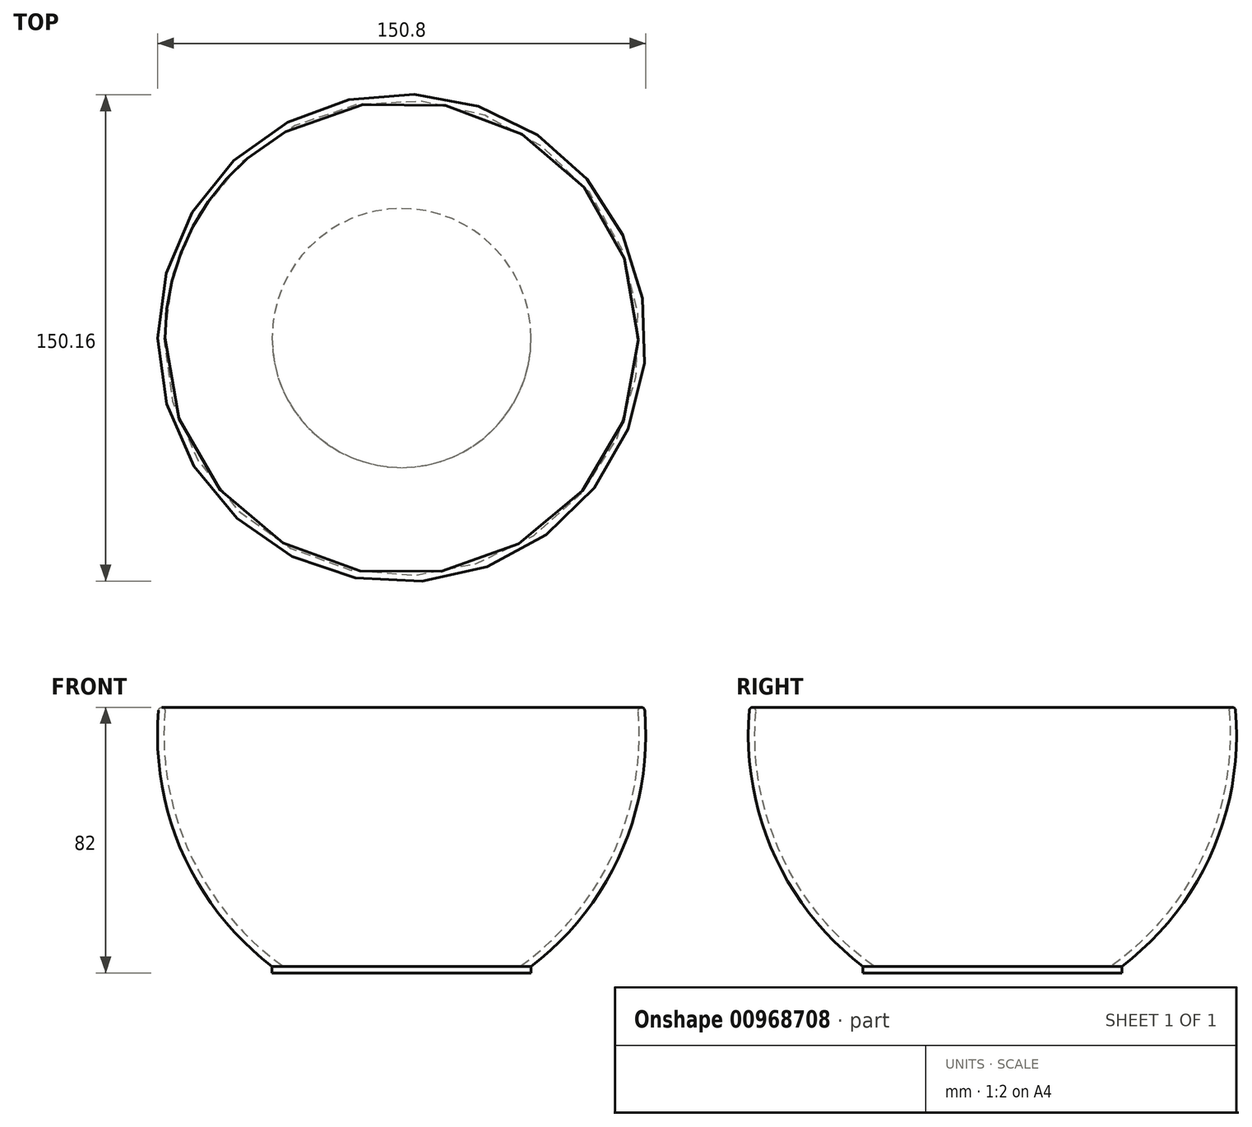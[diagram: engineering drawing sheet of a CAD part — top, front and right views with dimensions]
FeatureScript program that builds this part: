
annotation { "Feature Type Name" : "Feature", "Feature Type Description" : "" }
export const myFeature = defineFeature(function(context is Context, id is Id, definition is map)
    precondition{}
    {
        {
            var Q0;
            Q0=qCreatedBy(makeId("Front.planeOp"),FACE);
            var sketch = newSketch(context, id + "F0", { "sketchPlane" : qUnion([Q0])});
            skLineSegment(sketch, "E0.bottom", {"start": v(0, -82) * mm, "end": v(-40, -82) * mm});
            skLineSegment(sketch, "E0.top", {"start": v(0, -80) * mm, "end": v(-40, -80) * mm});
            skLineSegment(sketch, "E0.left", {"start": v(0, -82) * mm, "end": v(0, -80) * mm});
            skLineSegment(sketch, "E0.right", {"start": v(-40, -82) * mm, "end": v(-40, -80) * mm});
            skLineSegment(sketch, "E1", {"start": v(0, 0) * mm, "end": v(-75, 0) * mm, "construction": true});
            skArc(sketch, "E2", {"start": v(-75, 0) * mm, "mid": v(-67.85, -44.53) * mm, "end": v(-40, -80) * mm});
            skLineSegment(sketch, "E3", {"start": v(0, 0) * mm, "end": v(0, -87.47) * mm, "construction": true});
            skArc(sketch, "E4.0", {"start": v(-73, 0) * mm, "mid": v(-65.51, -44.86) * mm, "end": v(-36.64, -80) * mm});
            skLineSegment(sketch, "E5", {"start": v(-73, 0) * mm, "end": v(-75, 0) * mm});
            skSolve(sketch);
        }
        {
            var Q0;
            {var subQ0=sQuery(id+"F0.wireOp",EDGE,"E2");Q0=makeQuery(id+"F0.imprint","IMPRINT",FACE,{"disambiguationData":[TD([[makeQuery(id+"F0.imprint","IMPRINT",EDGE,{"derivedFrom":subQ0}),1.0]])]});}
            var Q1;
            Q1=makeQuery(id+"F0.imprint","IMPRINT",FACE,{"disambiguationData":[TD([[makeQuery(id+"F0.imprint","IMPRINT",EDGE,{"derivedFrom":sQuery(id+"F0.wireOp",EDGE,"E0.bottom")}),-1.0]])]});
            var Q2;
            Q2=sQuery(id+"F0.wireOp",EDGE,"E3");
            revolve(context, id + "F1", {"surfaceOperationType" : NewSurfaceOperationType.NEW, "entities" : qUnion([Q0, Q1]), "axis" : qUnion([Q2]), "revolveType" : RevolveType.FULL});
        }
        {
            var Q0;
            Q0=makeQuery(id+"F1.opRevolve","SWEPT_EDGE",EDGE,{"disambiguationData":[OSD([sQuery(id+"F0.wireOp",EDGE,"E4.0"),sQuery(id+"F0.wireOp",EDGE,"E5")])]});
            var Q1;
            Q1=makeQuery(id+"F1.opRevolve","SWEPT_EDGE",EDGE,{"disambiguationData":[OSD([sQuery(id+"F0.wireOp",EDGE,"E2"),sQuery(id+"F0.wireOp",EDGE,"E5")])]});
            fillet(context, id + "F2", {"entities" : qUnion([Q0, Q1]), "radius" : 1 * mm, "tangentPropagation" : true, "allowEdgeOverflow" : false});
        }
        {
            var Q0;
            Q0=makeQuery(id+"F1.opRevolve","SWEPT_EDGE",EDGE,{"disambiguationData":[OSD([sQuery(id+"F0.wireOp",EDGE,"E0.top"),sQuery(id+"F0.wireOp",EDGE,"E4.0")])]});
            fillet(context, id + "F3", {"entities" : qUnion([Q0]), "radius" : 1 * mm, "tangentPropagation" : true, "allowEdgeOverflow" : false});
        }
    });
